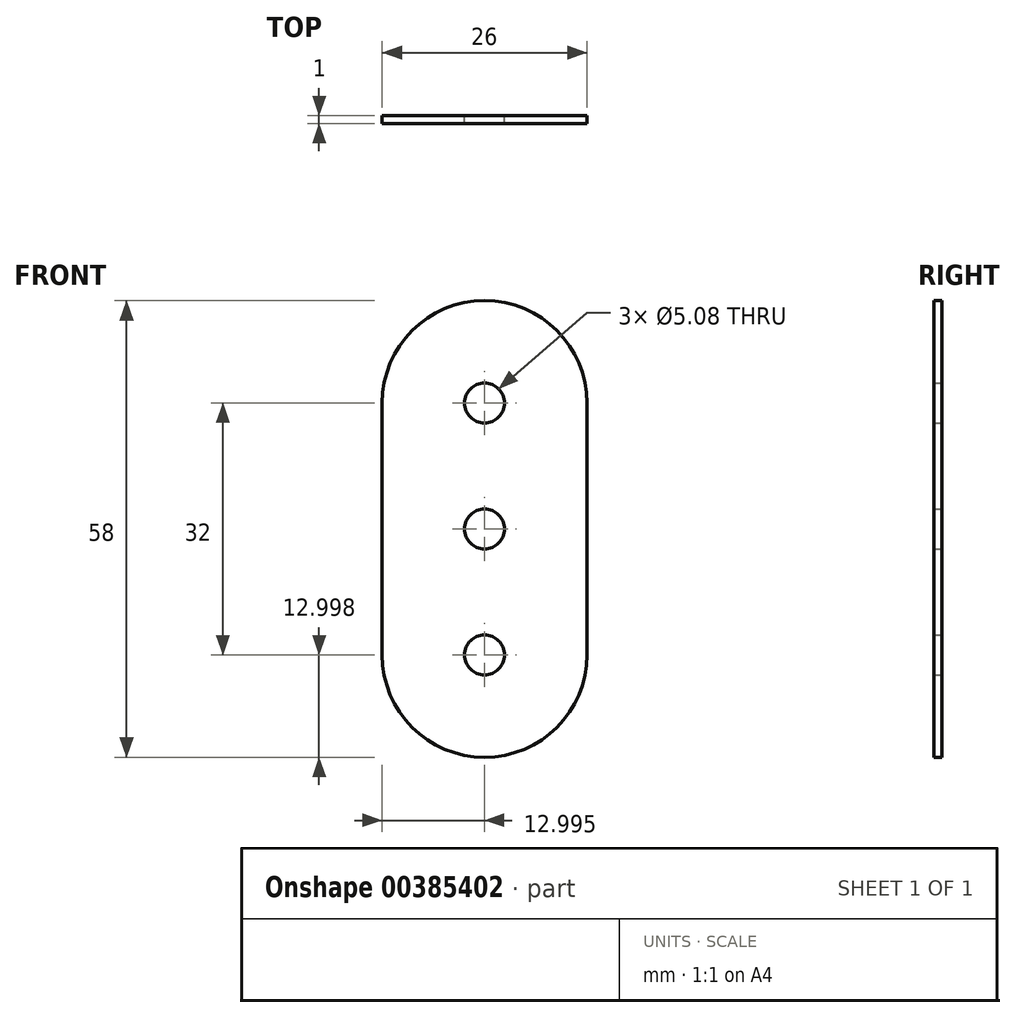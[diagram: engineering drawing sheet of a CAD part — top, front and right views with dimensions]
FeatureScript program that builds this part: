
annotation { "Feature Type Name" : "Feature", "Feature Type Description" : "" }
export const myFeature = defineFeature(function(context is Context, id is Id, definition is map)
    precondition{}
    {
        {
            var Q0;
            Q0=qCreatedBy(makeId("Front.planeOp"),FACE);
            var sketch = newSketch(context, id + "F0", { "sketchPlane" : qUnion([Q0])});
            skLineSegment(sketch, "E0", {"start": v(-14.84, 31.94) * mm, "end": v(-14.84, -0.06) * mm});
            skLineSegment(sketch, "E1", {"start": v(11.16, -0.06) * mm, "end": v(11.16, 31.94) * mm});
            skCircle(sketch, "E2", {"center": v(-1.84, 31.94) * mm, "radius": 2.54 * mm});
            skCircle(sketch, "E3", {"center": v(-1.84, -0.06) * mm, "radius": 2.54 * mm});
            skPoint(sketch, "E4", {"position": v(-1.84, 15.94) * mm});
            skCircle(sketch, "E5", {"center": v(-1.84, 15.94) * mm, "radius": 2.54 * mm});
            skCircle(sketch, "E6", {"center": v(-1.84, 31.94) * mm, "radius": 13 * mm});
            skCircle(sketch, "E7", {"center": v(-1.84, -0.06) * mm, "radius": 13 * mm});
            skSolve(sketch);
        }
        {
            var Q0;
            Q0=qSketchRegion(id+"F0",true);
            extrude(context, id + "F1", {"entities" : qUnion([Q0]), "depth" : 1 * mm});
        }
    });
